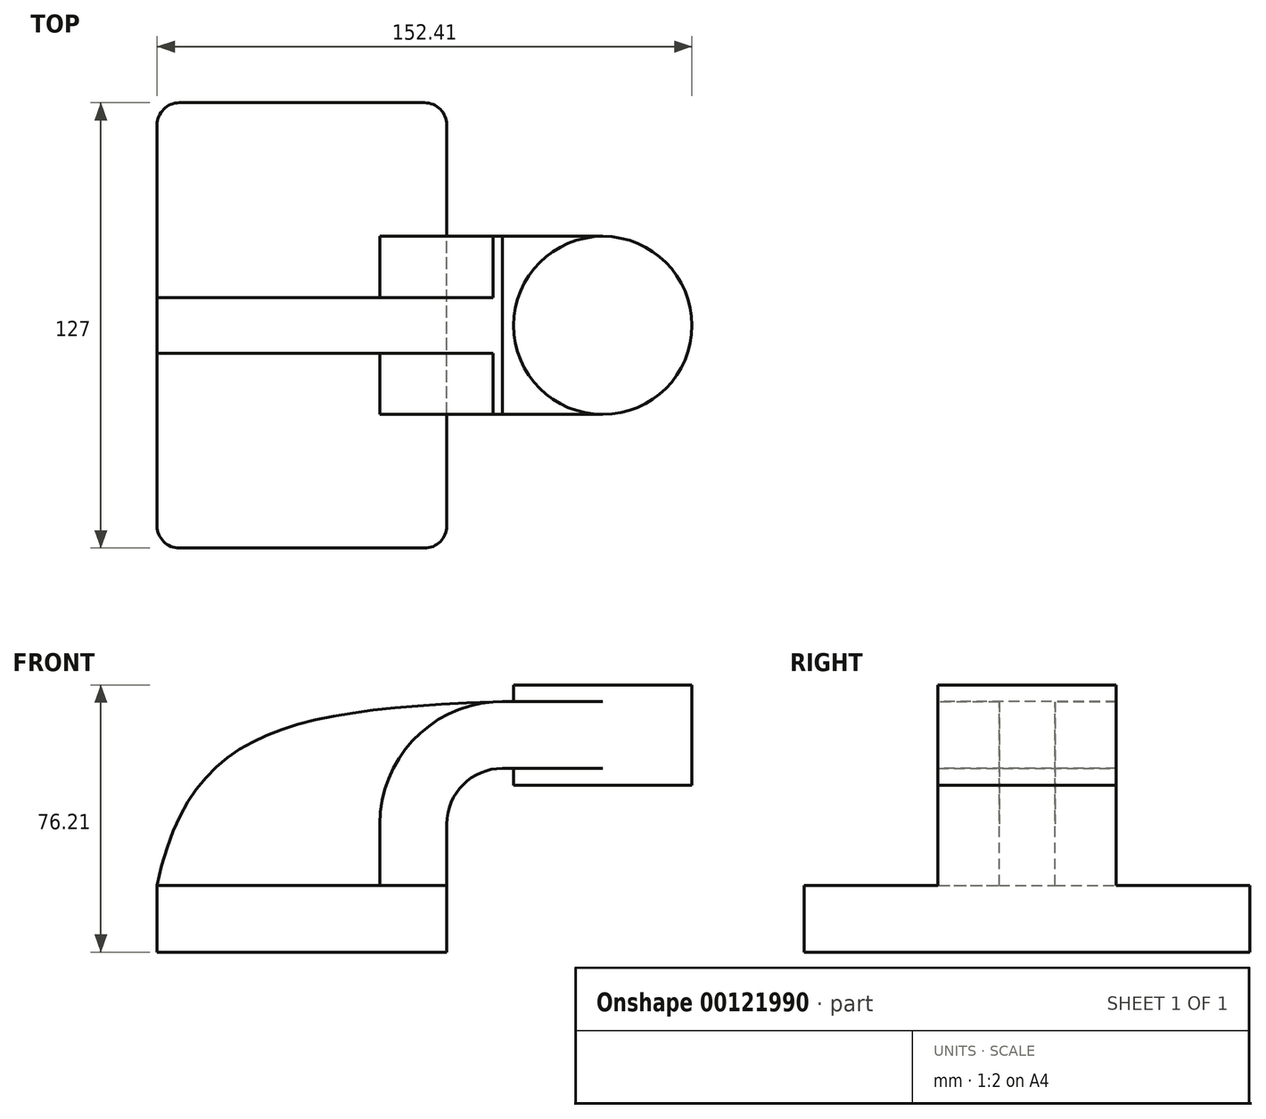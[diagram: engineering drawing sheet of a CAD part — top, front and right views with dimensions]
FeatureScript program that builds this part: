
annotation { "Feature Type Name" : "Feature", "Feature Type Description" : "" }
export const myFeature = defineFeature(function(context is Context, id is Id, definition is map)
    precondition{}
    {
        {
            var Q0;
            Q0=qCreatedBy(makeId("Front.planeOp"),FACE);
            var sketch = newSketch(context, id + "F0", { "sketchPlane" : qUnion([Q0])});
            skLineSegment(sketch, "E0.bottom", {"start": v(-41.27, -9.53) * mm, "end": v(41.28, -9.53) * mm});
            skLineSegment(sketch, "E0.top", {"start": v(-41.28, 9.53) * mm, "end": v(41.28, 9.53) * mm});
            skLineSegment(sketch, "E0.left", {"start": v(-41.28, -9.53) * mm, "end": v(-41.28, 9.53) * mm});
            skLineSegment(sketch, "E0.right", {"start": v(41.28, -9.53) * mm, "end": v(41.28, 9.53) * mm});
            skPoint(sketch, "E0.middle", {"position": v(0, 0) * mm});
            skLineSegment(sketch, "E1.bottom", {"start": v(111.12, 38.1) * mm, "end": v(60.32, 38.1) * mm});
            skLineSegment(sketch, "E1.top", {"start": v(111.12, 66.67) * mm, "end": v(60.32, 66.67) * mm});
            skLineSegment(sketch, "E1.left", {"start": v(111.12, 38.1) * mm, "end": v(111.12, 66.67) * mm});
            skLineSegment(sketch, "E1.right", {"start": v(60.32, 38.1) * mm, "end": v(60.32, 66.67) * mm});
            skPoint(sketch, "E1.middle", {"position": v(85.72, 52.39) * mm});
            skLineSegment(sketch, "E2", {"start": v(41.28, 9.53) * mm, "end": v(41.28, 27) * mm});
            skArc(sketch, "E3", {"start": v(41.27, 27) * mm, "mid": v(45.92, 38.23) * mm, "end": v(57.15, 42.88) * mm});
            skLineSegment(sketch, "E4", {"start": v(57.15, 42.88) * mm, "end": v(85.72, 42.88) * mm});
            skLineSegment(sketch, "E5.0", {"start": v(57.15, 61.93) * mm, "end": v(85.72, 61.93) * mm});
            skArc(sketch, "E5.1", {"start": v(22.22, 27) * mm, "mid": v(32.45, 51.7) * mm, "end": v(57.15, 61.93) * mm});
            skLineSegment(sketch, "E5.2", {"start": v(22.22, 9.53) * mm, "end": v(22.22, 27) * mm});
            skLineSegment(sketch, "E6", {"start": v(85.72, 66.67) * mm, "end": v(85.72, 38.1) * mm});
            skFitSpline(sketch, "E7", {"points": [v(-41.27, 9.52) * mm, v(57.15, 61.93) * mm], "startDerivative": vector(28.02, 135.03) * mm, "endDerivative": vector(182.3, 6.97) * mm});
            skSolve(sketch);
        }
        {
            var Q0;
            Q0=makeQuery(id+"F0.imprint","IMPRINT",FACE,{"disambiguationData":[TD([[makeQuery(id+"F0.imprint","IMPRINT",EDGE,{"derivedFrom":sQuery(id+"F0.wireOp",EDGE,"E0.bottom")}),1.0]])]});
            extrude(context, id + "F1", {"entities" : qUnion([Q0]), "endBound" : BoundingType.SYMMETRIC, "depth" : 127 * mm});
        }
        {
            var Q0;
            {var subQ1=sQuery(id+"F0.wireOp",EDGE,"E2");Q0=makeQuery(id+"F0.imprint","IMPRINT",FACE,{"disambiguationData":[TD([[makeQuery(id+"F0.imprint","IMPRINT",EDGE,{"derivedFrom":subQ1}),1.0]])]});}
            var Q1;
            {var subQ0=sQuery(id+"F0.wireOp",EDGE,"E4");var subQ1=sQuery(id+"F0.wireOp",EDGE,"E1.right");var subQ2=makeQuery(id+"F0.imprint","INTERSECT",VERTEX,{"derivedFrom":[subQ1,subQ0]});Q1=makeQuery(id+"F0.imprint","IMPRINT",FACE,{"disambiguationData":[TD([[makeQuery(id+"F0.imprint","IMPRINT",EDGE,{"disambiguationData":[TD([[subQ2,-1.0]])],"derivedFrom":subQ1}),-1.0]])]});}
            extrude(context, id + "F2", {"entities" : qUnion([Q0, Q1]), "operationType" : NewBodyOperationType.ADD, "endBound" : BoundingType.SYMMETRIC, "depth" : 50.8 * mm});
        }
        {
            var Q0;
            {var subQ0=sQuery(id+"F0.wireOp",EDGE,"E1.left");Q0=makeQuery(id+"F0.imprint","IMPRINT",FACE,{"disambiguationData":[TD([[makeQuery(id+"F0.imprint","IMPRINT",EDGE,{"derivedFrom":subQ0}),1.0]])]});}
            var Q1;
            Q1=sQuery(id+"F0.wireOp",EDGE,"E6");
            revolve(context, id + "F3", {"operationType" : NewBodyOperationType.ADD, "entities" : qUnion([Q0]), "axis" : qUnion([Q1]), "revolveType" : RevolveType.FULL});
        }
        {
            var Q0;
            {var subQ3=sQuery(id+"F0.wireOp",EDGE,"E5.2");Q0=makeQuery(id+"F0.imprint","IMPRINT",FACE,{"disambiguationData":[TD([[makeQuery(id+"F0.imprint","IMPRINT",EDGE,{"derivedFrom":subQ3}),1.0]])]});}
            extrude(context, id + "F4", {"entities" : qUnion([Q0]), "operationType" : NewBodyOperationType.ADD, "endBound" : BoundingType.SYMMETRIC, "depth" : 15.88 * mm});
        }
        {
            var Q0;
            Q0=makeQuery(id+"F1.opExtrude","CAP_EDGE",EDGE,{"disambiguationData":[OSD([sQuery(id+"F0.wireOp",EDGE,"E0.right")])],"isStart":false});
            var Q1;
            Q1=makeQuery(id+"F1.opExtrude","CAP_EDGE",EDGE,{"disambiguationData":[OSD([sQuery(id+"F0.wireOp",EDGE,"E0.left")])],"isStart":false});
            var Q2;
            Q2=makeQuery(id+"F1.opExtrude","CAP_EDGE",EDGE,{"disambiguationData":[OSD([sQuery(id+"F0.wireOp",EDGE,"E0.right")])],"isStart":true});
            var Q3;
            Q3=makeQuery(id+"F1.opExtrude","CAP_EDGE",EDGE,{"disambiguationData":[OSD([sQuery(id+"F0.wireOp",EDGE,"E0.left")])],"isStart":true});
            fillet(context, id + "F5", {"entities" : qUnion([Q0, Q1, Q2, Q3]), "radius" : 6.35 * mm, "tangentPropagation" : true, "allowEdgeOverflow" : false});
        }
    });
